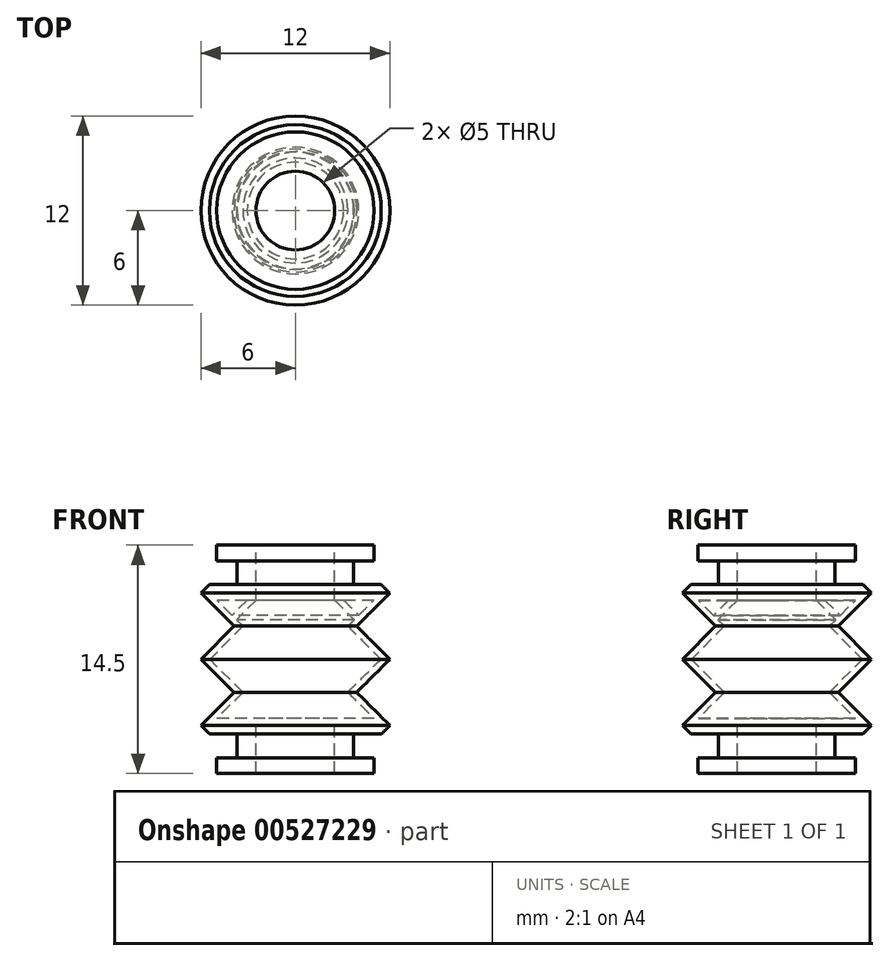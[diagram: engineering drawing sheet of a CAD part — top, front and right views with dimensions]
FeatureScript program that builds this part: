
annotation { "Feature Type Name" : "Feature", "Feature Type Description" : "" }
export const myFeature = defineFeature(function(context is Context, id is Id, definition is map)
    precondition{}
    {
        {
            var Q0;
            Q0=qCreatedBy(makeId("Front.planeOp"),FACE);
            var sketch = newSketch(context, id + "F0", { "sketchPlane" : qUnion([Q0])});
            skLineSegment(sketch, "E0", {"start": v(-2.5, 7.25) * mm, "end": v(-5, 7.25) * mm});
            skLineSegment(sketch, "E1", {"start": v(-5, 7.25) * mm, "end": v(-5, 6.25) * mm});
            skLineSegment(sketch, "E2", {"start": v(-5, 6.25) * mm, "end": v(-3.7, 6.25) * mm});
            skLineSegment(sketch, "E3", {"start": v(-3.7, 6.25) * mm, "end": v(-3.7, 4.75) * mm});
            skLineSegment(sketch, "E4", {"start": v(-5.45, 4.75) * mm, "end": v(-6, 4.2) * mm});
            skLineSegment(sketch, "E5", {"start": v(-6, 4.2) * mm, "end": v(-3.9, 2.1) * mm});
            skLineSegment(sketch, "E6", {"start": v(-3.9, 2.1) * mm, "end": v(-6, 0) * mm});
            skLineSegment(sketch, "E7", {"start": v(-3.7, 4.75) * mm, "end": v(-5.45, 4.75) * mm});
            skLineSegment(sketch, "E8", {"start": v(0, 8.81) * mm, "end": v(0, -10.41) * mm, "construction": true});
            skLineSegment(sketch, "E9", {"start": v(-5.43, 0) * mm, "end": v(-3.33, 2.1) * mm});
            skLineSegment(sketch, "E10", {"start": v(-3.33, 2.1) * mm, "end": v(-3.74, 2.5) * mm});
            skLineSegment(sketch, "E11", {"start": v(-2.5, 7.25) * mm, "end": v(-2.5, 3.75) * mm});
            skLineSegment(sketch, "E12.MirrorCS", {"start": v(-2.5, -7.25) * mm, "end": v(-5, -7.25) * mm});
            skLineSegment(sketch, "E13.MirrorCS", {"start": v(-5, -7.25) * mm, "end": v(-5, -6.25) * mm});
            skLineSegment(sketch, "E14.MirrorCS", {"start": v(-2.5, -7.25) * mm, "end": v(-2.5, -3.75) * mm});
            skLineSegment(sketch, "E15.MirrorCS", {"start": v(-3.7, -6.25) * mm, "end": v(-3.7, -4.75) * mm});
            skLineSegment(sketch, "E16.MirrorCS", {"start": v(-2.5, -3.75) * mm, "end": v(-4.98, -3.75) * mm});
            skLineSegment(sketch, "E17.MirrorCS", {"start": v(-5.45, -4.75) * mm, "end": v(-6, -4.2) * mm});
            skLineSegment(sketch, "E18.MirrorCS", {"start": v(-6, -4.2) * mm, "end": v(-3.9, -2.1) * mm});
            skLineSegment(sketch, "E19.MirrorCS", {"start": v(-3.33, -2.1) * mm, "end": v(-4.98, -3.75) * mm});
            skLineSegment(sketch, "E20.MirrorCS", {"start": v(-5.43, 0) * mm, "end": v(-3.33, -2.1) * mm});
            skLineSegment(sketch, "E21.MirrorCS", {"start": v(-3.9, -2.1) * mm, "end": v(-6, 0) * mm});
            skLineSegment(sketch, "E22.MirrorCS", {"start": v(-3.7, -4.75) * mm, "end": v(-5.45, -4.75) * mm});
            skLineSegment(sketch, "E23", {"start": v(-5, -6.25) * mm, "end": v(-3.7, -6.25) * mm});
            skLineSegment(sketch, "E24.trimOffspring", {"start": v(-3.07, 3.75) * mm, "end": v(-4.98, 3.75) * mm});
            skLineSegment(sketch, "E25", {"start": v(-3.07, 3.75) * mm, "end": v(-4.02, 2.8) * mm});
            skLineSegment(sketch, "E26", {"start": v(-3.74, 2.5) * mm, "end": v(-2.5, 3.75) * mm});
            skLineSegment(sketch, "E27.trimOffspring", {"start": v(-4.02, 2.8) * mm, "end": v(-4.98, 3.75) * mm});
            skSolve(sketch);
        }
        {
            var Q0;
            Q0=makeQuery(id+"F0.imprint","IMPRINT",FACE,{"disambiguationData":[TD([[makeQuery(id+"F0.imprint","IMPRINT",EDGE,{"derivedFrom":sQuery(id+"F0.wireOp",EDGE,"E0")}),1.0]])]});
            var Q1;
            Q1=sQuery(id+"F0.wireOp",EDGE,"E8");
            revolve(context, id + "F1", {"entities" : qUnion([Q0]), "axis" : qUnion([Q1]), "revolveType" : RevolveType.FULL});
        }
    });
